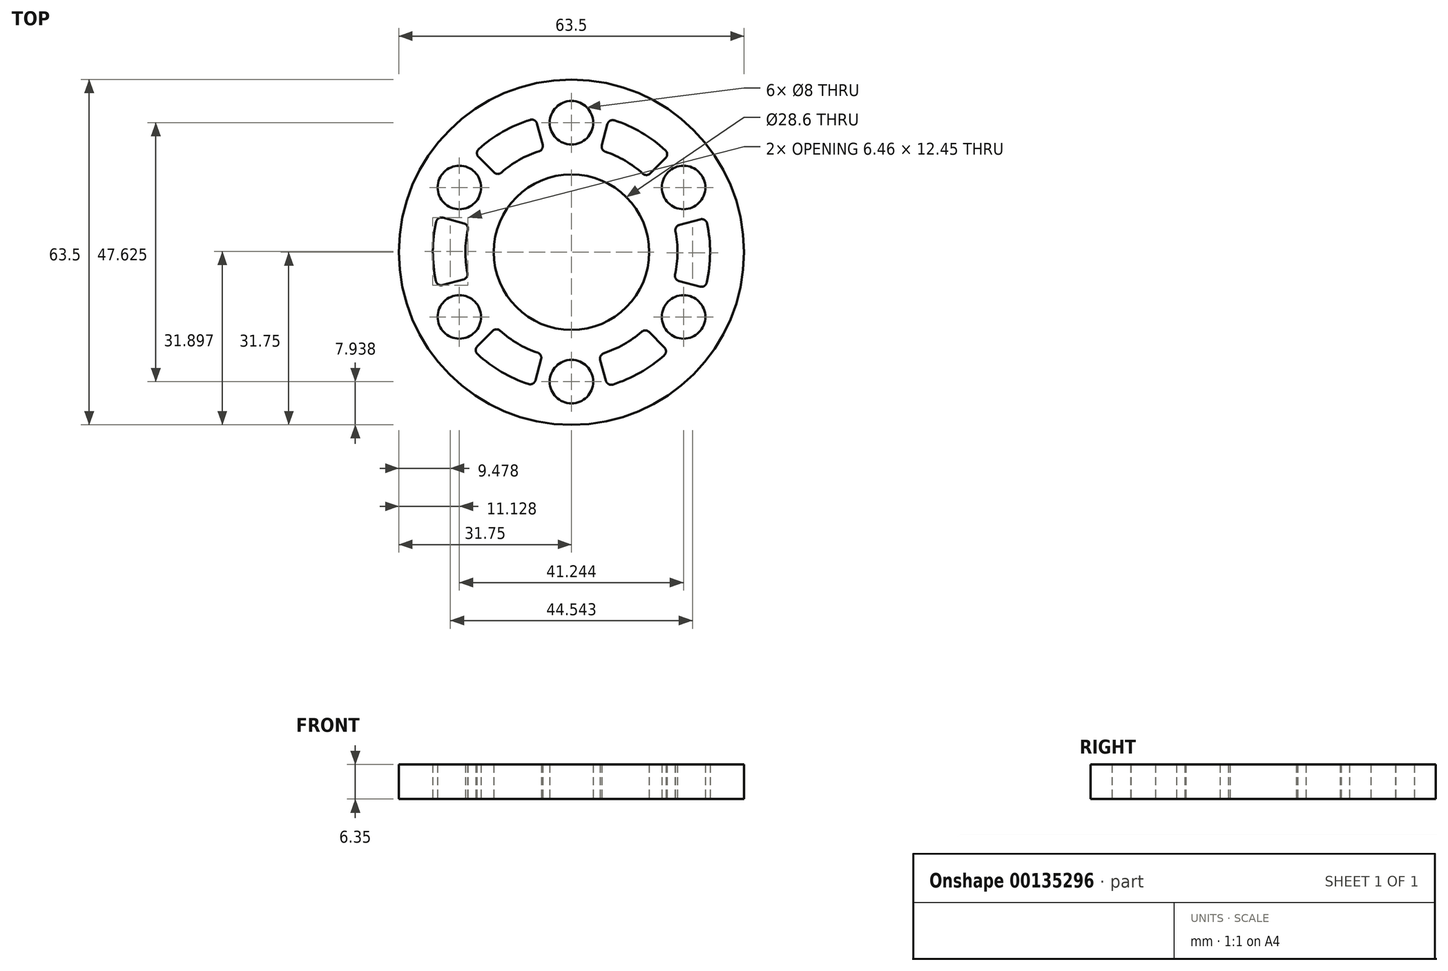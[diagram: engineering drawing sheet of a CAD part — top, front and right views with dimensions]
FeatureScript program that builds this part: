
annotation { "Feature Type Name" : "Feature", "Feature Type Description" : "" }
export const myFeature = defineFeature(function(context is Context, id is Id, definition is map)
    precondition{}
    {
        {
            var Q0;
            Q0=qCreatedBy(makeId("Top.planeOp"),FACE);
            var sketch = newSketch(context, id + "F0", { "sketchPlane" : qUnion([Q0])});
            skCircle(sketch, "E0", {"center": v(0, 0) * mm, "radius": 14.3 * mm});
            skCircle(sketch, "E1", {"center": v(0, 0) * mm, "radius": 31.75 * mm});
            skCircle(sketch, "E2", {"center": v(0, 23.81) * mm, "radius": 4 * mm});
            skCircle(sketch, "E3.1.0", {"center": v(-20.62, 11.9) * mm, "radius": 4 * mm});
            skCircle(sketch, "E3.2.0", {"center": v(-20.62, -11.9) * mm, "radius": 4 * mm});
            skCircle(sketch, "E3.3.0", {"center": v(0, -23.81) * mm, "radius": 4 * mm});
            skCircle(sketch, "E3.4.0", {"center": v(20.62, -11.9) * mm, "radius": 4 * mm});
            skCircle(sketch, "E3.5.0", {"center": v(20.62, 11.9) * mm, "radius": 4 * mm});
            skLineSegment(sketch, "E4", {"start": v(14.48, 14.48) * mm, "end": v(17.32, 17.32) * mm});
            skLineSegment(sketch, "E5", {"start": v(5.59, 19.68) * mm, "end": v(6.63, 23.56) * mm});
            skLineSegment(sketch, "E6", {"start": v(0, 0) * mm, "end": v(0, 46.03) * mm, "construction": true});
            skCircle(sketch, "E7", {"center": v(0, 0) * mm, "radius": 23.81 * mm, "construction": true});
            skArc(sketch, "E8", {"start": v(6.23, 18.49) * mm, "mid": v(9.88, 16.82) * mm, "end": v(13.11, 14.44) * mm});
            skArc(sketch, "E9", {"start": v(7.89, 24.25) * mm, "mid": v(12.89, 22) * mm, "end": v(17.29, 18.75) * mm});
            skPoint(sketch, "E10.visualSharp", {"position": v(6.9, 24.55) * mm});
            skArc(sketch, "E10.filletArc", {"start": v(7.89, 24.25) * mm, "mid": v(7.11, 24.18) * mm, "end": v(6.63, 23.56) * mm});
            skPoint(sketch, "E11.visualSharp", {"position": v(5.34, 18.76) * mm});
            skArc(sketch, "E11.filletArc", {"start": v(5.59, 19.68) * mm, "mid": v(5.67, 18.96) * mm, "end": v(6.23, 18.49) * mm});
            skPoint(sketch, "E12.visualSharp", {"position": v(13.8, 13.8) * mm});
            skArc(sketch, "E12.filletArc", {"start": v(13.11, 14.44) * mm, "mid": v(13.8, 14.19) * mm, "end": v(14.48, 14.48) * mm});
            skPoint(sketch, "E13.visualSharp", {"position": v(18.03, 18.03) * mm});
            skArc(sketch, "E13.filletArc", {"start": v(17.32, 17.32) * mm, "mid": v(17.6, 18.04) * mm, "end": v(17.29, 18.75) * mm});
            skLineSegment(sketch, "E14.1.0", {"start": v(-14.25, 14.68) * mm, "end": v(-17.1, 17.52) * mm});
            skPoint(sketch, "E14.1.1", {"position": v(-17.82, 18.24) * mm});
            skPoint(sketch, "E14.1.2", {"position": v(-5.05, 18.84) * mm});
            skArc(sketch, "E14.1.3", {"start": v(-12.9, 14.64) * mm, "mid": v(-9.63, 16.97) * mm, "end": v(-5.95, 18.58) * mm});
            skArc(sketch, "E14.1.4", {"start": v(-14.25, 14.68) * mm, "mid": v(-13.58, 14.39) * mm, "end": v(-12.9, 14.64) * mm});
            skArc(sketch, "E14.1.5", {"start": v(-17.06, 18.96) * mm, "mid": v(-17.38, 18.25) * mm, "end": v(-17.1, 17.52) * mm});
            skArc(sketch, "E14.1.6", {"start": v(-17.06, 18.96) * mm, "mid": v(-12.61, 22.16) * mm, "end": v(-7.6, 24.35) * mm});
            skArc(sketch, "E14.1.7", {"start": v(-5.95, 18.58) * mm, "mid": v(-5.39, 19.05) * mm, "end": v(-5.3, 19.78) * mm});
            skLineSegment(sketch, "E14.1.8", {"start": v(-5.3, 19.78) * mm, "end": v(-6.34, 23.66) * mm});
            skArc(sketch, "E14.1.9", {"start": v(-6.34, 23.66) * mm, "mid": v(-6.82, 24.27) * mm, "end": v(-7.6, 24.35) * mm});
            skPoint(sketch, "E14.1.10", {"position": v(-6.6, 24.63) * mm});
            skLineSegment(sketch, "E14.2.0", {"start": v(-19.84, -5) * mm, "end": v(-23.72, -6.04) * mm});
            skPoint(sketch, "E14.2.1", {"position": v(-24.7, -6.3) * mm});
            skPoint(sketch, "E14.2.2", {"position": v(-18.84, 5.05) * mm});
            skArc(sketch, "E14.2.3", {"start": v(-19.12, -3.85) * mm, "mid": v(-19.5, 0.14) * mm, "end": v(-19.06, 4.13) * mm});
            skArc(sketch, "E14.2.4", {"start": v(-19.84, -5) * mm, "mid": v(-19.25, -4.57) * mm, "end": v(-19.12, -3.85) * mm});
            skArc(sketch, "E14.2.5", {"start": v(-24.95, -5.3) * mm, "mid": v(-24.5, -5.93) * mm, "end": v(-23.72, -6.04) * mm});
            skArc(sketch, "E14.2.6", {"start": v(-24.95, -5.3) * mm, "mid": v(-25.5, 0.16) * mm, "end": v(-24.88, 5.6) * mm});
            skArc(sketch, "E14.2.7", {"start": v(-19.06, 4.13) * mm, "mid": v(-19.19, 4.86) * mm, "end": v(-19.78, 5.3) * mm});
            skLineSegment(sketch, "E14.2.8", {"start": v(-19.78, 5.3) * mm, "end": v(-23.66, 6.34) * mm});
            skArc(sketch, "E14.2.9", {"start": v(-23.66, 6.34) * mm, "mid": v(-24.43, 6.23) * mm, "end": v(-24.88, 5.6) * mm});
            skPoint(sketch, "E14.2.10", {"position": v(-24.63, 6.6) * mm});
            skLineSegment(sketch, "E14.3.0", {"start": v(-5.59, -19.68) * mm, "end": v(-6.63, -23.56) * mm});
            skPoint(sketch, "E14.3.1", {"position": v(-6.9, -24.55) * mm});
            skPoint(sketch, "E14.3.2", {"position": v(-13.8, -13.8) * mm});
            skArc(sketch, "E14.3.3", {"start": v(-6.23, -18.49) * mm, "mid": v(-9.88, -16.82) * mm, "end": v(-13.11, -14.44) * mm});
            skArc(sketch, "E14.3.4", {"start": v(-5.59, -19.68) * mm, "mid": v(-5.67, -18.96) * mm, "end": v(-6.23, -18.49) * mm});
            skArc(sketch, "E14.3.5", {"start": v(-7.89, -24.25) * mm, "mid": v(-7.11, -24.18) * mm, "end": v(-6.63, -23.56) * mm});
            skArc(sketch, "E14.3.6", {"start": v(-7.89, -24.25) * mm, "mid": v(-12.89, -22) * mm, "end": v(-17.29, -18.75) * mm});
            skArc(sketch, "E14.3.7", {"start": v(-13.11, -14.44) * mm, "mid": v(-13.8, -14.19) * mm, "end": v(-14.48, -14.48) * mm});
            skLineSegment(sketch, "E14.3.8", {"start": v(-14.48, -14.48) * mm, "end": v(-17.32, -17.32) * mm});
            skArc(sketch, "E14.3.9", {"start": v(-17.32, -17.32) * mm, "mid": v(-17.6, -18.04) * mm, "end": v(-17.29, -18.75) * mm});
            skPoint(sketch, "E14.3.10", {"position": v(-18.03, -18.03) * mm});
            skLineSegment(sketch, "E14.4.0", {"start": v(14.25, -14.68) * mm, "end": v(17.1, -17.52) * mm});
            skPoint(sketch, "E14.4.1", {"position": v(17.82, -18.24) * mm});
            skPoint(sketch, "E14.4.2", {"position": v(5.05, -18.84) * mm});
            skArc(sketch, "E14.4.3", {"start": v(12.9, -14.64) * mm, "mid": v(9.63, -16.97) * mm, "end": v(5.95, -18.58) * mm});
            skArc(sketch, "E14.4.4", {"start": v(14.25, -14.68) * mm, "mid": v(13.58, -14.39) * mm, "end": v(12.9, -14.64) * mm});
            skArc(sketch, "E14.4.5", {"start": v(17.06, -18.96) * mm, "mid": v(17.38, -18.25) * mm, "end": v(17.1, -17.52) * mm});
            skArc(sketch, "E14.4.6", {"start": v(17.06, -18.96) * mm, "mid": v(12.61, -22.16) * mm, "end": v(7.6, -24.35) * mm});
            skArc(sketch, "E14.4.7", {"start": v(5.95, -18.58) * mm, "mid": v(5.39, -19.05) * mm, "end": v(5.3, -19.78) * mm});
            skLineSegment(sketch, "E14.4.8", {"start": v(5.3, -19.78) * mm, "end": v(6.34, -23.66) * mm});
            skArc(sketch, "E14.4.9", {"start": v(6.34, -23.66) * mm, "mid": v(6.82, -24.27) * mm, "end": v(7.6, -24.35) * mm});
            skPoint(sketch, "E14.4.10", {"position": v(6.6, -24.63) * mm});
            skLineSegment(sketch, "E14.5.0", {"start": v(19.84, 5) * mm, "end": v(23.72, 6.04) * mm});
            skPoint(sketch, "E14.5.1", {"position": v(24.7, 6.3) * mm});
            skPoint(sketch, "E14.5.2", {"position": v(18.84, -5.05) * mm});
            skArc(sketch, "E14.5.3", {"start": v(19.12, 3.85) * mm, "mid": v(19.5, -0.14) * mm, "end": v(19.06, -4.13) * mm});
            skArc(sketch, "E14.5.4", {"start": v(19.84, 5) * mm, "mid": v(19.25, 4.57) * mm, "end": v(19.12, 3.85) * mm});
            skArc(sketch, "E14.5.5", {"start": v(24.95, 5.3) * mm, "mid": v(24.5, 5.93) * mm, "end": v(23.72, 6.04) * mm});
            skArc(sketch, "E14.5.6", {"start": v(24.95, 5.3) * mm, "mid": v(25.5, -0.16) * mm, "end": v(24.88, -5.6) * mm});
            skArc(sketch, "E14.5.7", {"start": v(19.06, -4.13) * mm, "mid": v(19.19, -4.86) * mm, "end": v(19.78, -5.3) * mm});
            skLineSegment(sketch, "E14.5.8", {"start": v(19.78, -5.3) * mm, "end": v(23.66, -6.34) * mm});
            skArc(sketch, "E14.5.9", {"start": v(23.66, -6.34) * mm, "mid": v(24.43, -6.23) * mm, "end": v(24.88, -5.6) * mm});
            skPoint(sketch, "E14.5.10", {"position": v(24.63, -6.6) * mm});
            skSolve(sketch);
        }
        {
            var Q0;
            Q0=makeQuery(id+"F0.imprint","IMPRINT",FACE,{"disambiguationData":[TD([[makeQuery(id+"F0.imprint","IMPRINT",EDGE,{"derivedFrom":sQuery(id+"F0.wireOp",EDGE,"E0")}),-1.0]])]});
            extrude(context, id + "F1", {"entities" : qUnion([Q0]), "depth" : 6.35 * mm});
        }
    });
